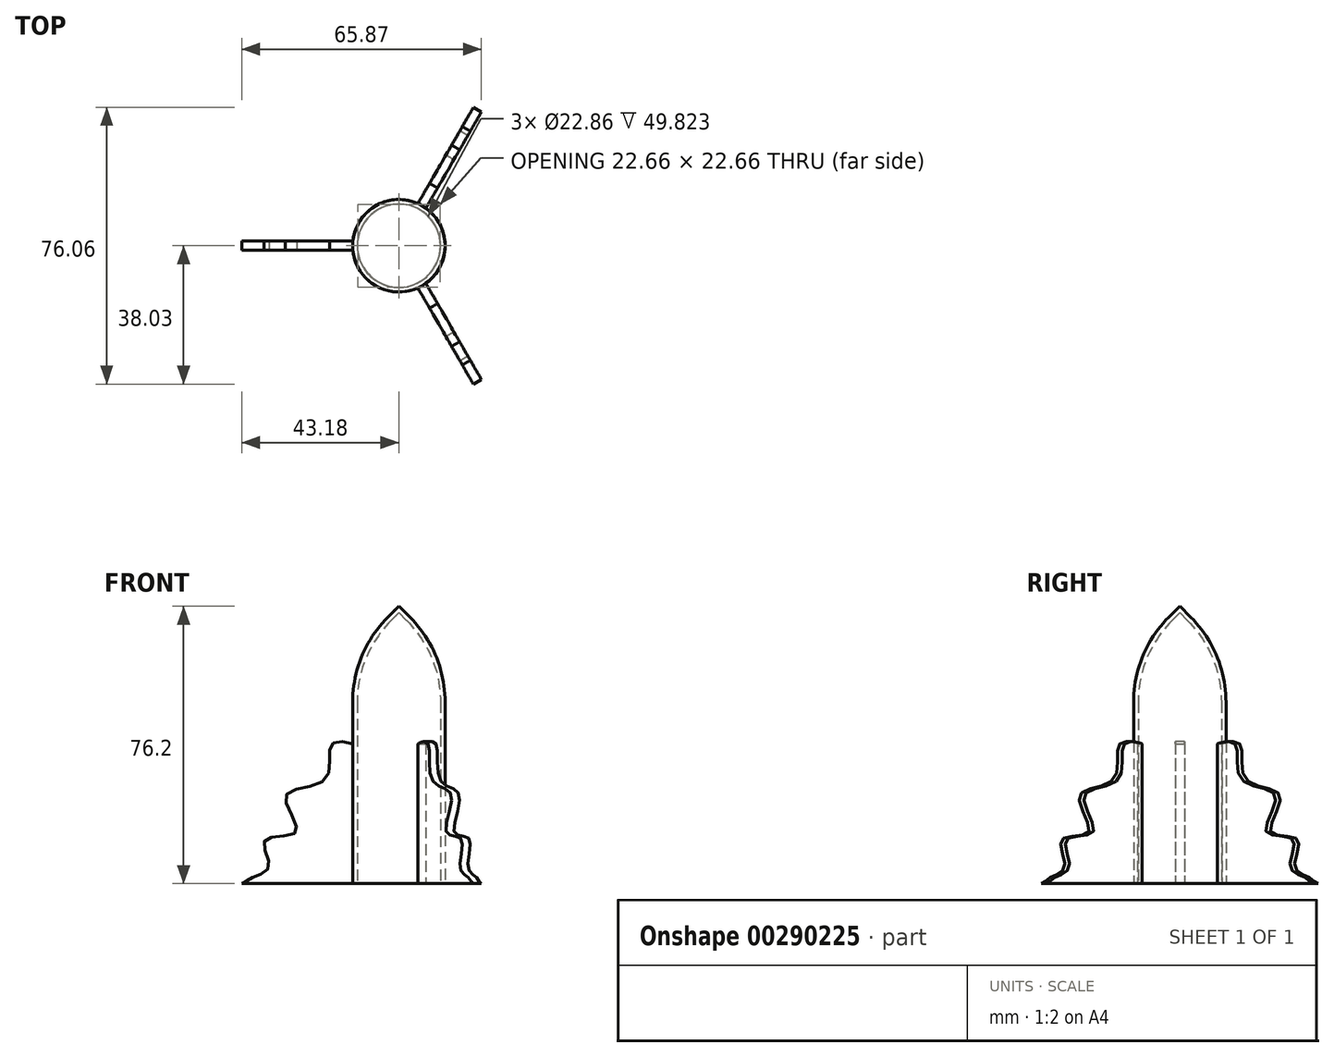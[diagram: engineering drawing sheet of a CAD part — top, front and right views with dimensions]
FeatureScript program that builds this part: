
annotation { "Feature Type Name" : "Feature", "Feature Type Description" : "" }
export const myFeature = defineFeature(function(context is Context, id is Id, definition is map)
    precondition{}
    {
        {
            var Q0;
            Q0=qCreatedBy(makeId("Top.planeOp"),FACE);
            var sketch = newSketch(context, id + "F0", { "sketchPlane" : qUnion([Q0])});
            skCircle(sketch, "E0", {"center": v(0, 0) * mm, "radius": 12.7 * mm});
            skSolve(sketch);
        }
        {
            var Q0;
            Q0 = qSketchRegion(id + "F0", true);
            extrude(context, id + "F1", {"entities" : qUnion([Q0]), "depth" : 76.2 * mm});
        }
        {
            var Q0;
            Q0=makeQuery(id+"F1.opExtrude","CAP_EDGE",EDGE,{"disambiguationData":[OSD([sQuery(id+"F0.wireOp",EDGE,"E0")])],"isStart":false});
            chamfer(context, id + "F2", {"entities" : qUnion([Q0]), "width" : 12.7 * mm, "tangentPropagation" : true});
        }
        {
            var Q0;
            {var subQ0=sQuery(id+"F0.wireOp",EDGE,"E0");Q0=makeQuery(id+"F2.opChamfer","BLEND_EDGE",EDGE,{"blendedFrom":[makeQuery(id+"F1.opExtrude","CAP_EDGE",EDGE,{"disambiguationData":[OSD([subQ0])],"isStart":false}),makeQuery(id+"F1.opExtrude","SWEPT_FACE",FACE,{"disambiguationData":[OSD([subQ0])]})],"blendedInto":[makeQuery(id+"F1.opExtrude","SWEPT_FACE",FACE,{"disambiguationData":[OSD([subQ0])]})]});}
            fillet(context, id + "F3", {"entities" : qUnion([Q0]), "radius" : 33.02 * mm, "tangentPropagation" : true, "allowEdgeOverflow" : false});
        }
        {
            var Q0;
            Q0=makeQuery(id+"F1.opExtrude","CAP_FACE",FACE,{"disambiguationData":[OSD([sQuery(id+"F0.wireOp",EDGE,"E0")])],"isStart":true});
            shell(context, id + "F4", {"entities" : qUnion([Q0]), "thickness" : 1.27 * mm});
        }
        {
            var Q0;
            Q0=qCreatedBy(makeId("Front.planeOp"),FACE);
            var sketch = newSketch(context, id + "F5", { "sketchPlane" : qUnion([Q0])});
            skLineSegment(sketch, "E1", {"start": v(-11.43, 0) * mm, "end": v(-11.43, 38.1) * mm});
            skFitSpline(sketch, "E2", {"points": [v(-11.43, 38.1) * mm, v(-18.57, 38.1) * mm, v(-20.24, 28.68) * mm, v(-31.1, 24.04) * mm, v(-28.19, 14.27) * mm, v(-36.74, 11.98) * mm, v(-35.77, 4.57) * mm, v(-40.56, 1.59) * mm, v(-43.18, 0) * mm], "startDerivative": vector(-65.15, 17.6) * mm, "endDerivative": vector(-45.05, -9.8) * mm});
            skLineSegment(sketch, "E3", {"start": v(-43.18, 0) * mm, "end": v(-11.43, 0) * mm});
            skSolve(sketch);
        }
        {
            var Q0;
            Q0 = qSketchRegion(id + "F5", true);
            extrude(context, id + "F6", {"entities" : qUnion([Q0]), "operationType" : NewBodyOperationType.ADD, "endBound" : BoundingType.SYMMETRIC, "depth" : 2.54 * mm});
        }
        {
            var Q0;
            Q0=makeQuery(id+"F1.opExtrude","SWEPT_BODY",BODY,{"disambiguationData":[OSD([sQuery(id+"F0.wireOp",EDGE,"E0")])]});
            var Q1;
            {var subQ0=sQuery(id+"F0.wireOp",EDGE,"E0");var subQ1=makeQuery(id+"F1.opExtrude","SWEPT_FACE",FACE,{"disambiguationData":[OSD([subQ0])]});Q1=makeQuery(id+"F3.opFillet","BLEND_EDGE",EDGE,{"blendedFrom":[makeQuery(id+"F2.opChamfer","BLEND_EDGE",EDGE,{"blendedFrom":[makeQuery(id+"F1.opExtrude","CAP_EDGE",EDGE,{"disambiguationData":[OSD([subQ0])],"isStart":false}),subQ1],"blendedInto":[subQ1]}),subQ1],"blendedInto":[subQ1]});}
            circularPattern(context, id + "F7", {"entities" : qUnion([Q0]), "axis" : qUnion([Q1]), "angle" : 360 * degree, "instanceCount" : 3, "equalSpace" : true});
        }
    });
